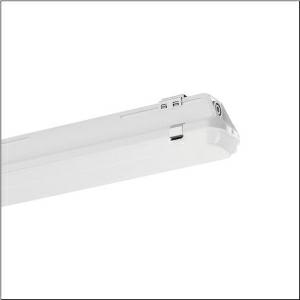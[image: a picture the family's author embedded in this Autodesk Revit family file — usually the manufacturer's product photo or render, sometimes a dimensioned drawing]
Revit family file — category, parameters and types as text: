
# Revit family: monsun_21_51fb107l440k005
name_source: partatom
category: Lighting Fixtures
units: mm (PartAtom-declared; Revit-internal decimal feet)

## family parameters
Cut with Voids When Loaded = No
Host = Face
Light Source = No
Part Type = Normal
Room Calculation Point = No
Round Connector Dimension = Use Diameter
Shared = No

## types (1)
- Monsun 21 (1 x LED, 4350 lm, 24.7 W, 4000K)
    Apparent Load = 25 VA
    CIE Flux Codes = 46 76 93 94 100
    Color Rendering = 80
    Color Temperature = 4000K
    Default Elevation = 1800 mm
    Description = Monsun 21, damp-proof luminaire, chain hanger, primary optical cover: enclosure, of PMMA, light emission: direct distribution, primary light characteristic: symmetric, installation type: vertical mounting, horizontal mounting, surface-mounted, suspended mounting, LED, rated luminous flux: 4.350lm, luminous efficacy: 176lm/W, light colour: 840, colour temperature: 4000K, control gear: ON/OFF, with terminal, 3-pole, max. 2.5mm², through-wiring: 5x 2.5mm², mains connection: 220..240V, AC, 50/60Hz, rated input power: 25W, housing, of glass-fibre reinforced plastic, uncoated, bright grey, incl. chain hanger, length: 1.299mm, width: 90mm, height: 88mm, clip for enclosure, of stainless steel (V2A), ceiling mounting element, of stainless steel (V2A), chain hanger, of stainless steel (V2A), protection rating (complete): IP66, insulation class (complete): insulation class I (protective earthing), certification: CE, ENEC, VDE, UKCA, protection symbol: D, impact resistance: IK04, permissible operating ambient temperature: -25..+35°C, standard: EN 50419, EN 60598-2-1, corresponds to IFS (International Featured Standards) requirements for safety and quality in the food industry, for indoor or canopied outdoor use, no direct snow, no direct sun, no direct rain, LABS conformity tested according to VDMA 24364:2018-05, contact your sales advisor before using the luminaires in applications with unclear chemical exposure, large temperature fluctuations or condensation-forming humidity, packaging unit: 1 piece
    Height = 88 mm
    Lamp = 1 x LED
    Lamp Light Flux = 4350 lm
    Lamp Power = 24.7 W
    Lamp count = 1
    Length = 1299 mm
    Luminous efficacy = 176 lm/W
    Manufacturer = Siteco
    ModVariant = No
    Model = 51FB107L440K005
    Mounting Place = Ceiling
    Mounting Type = Surface mounted
    Number of Poles = 1
    OnlyDefault = Yes
    Power Factor = 1
    Product Name = Monsun 21
    Product group = damp-proof luminaire
    ProductGroupID = 300
    Protection Class = Protection class I
    Protection Degree = IP 66
    RLX_Detail_Level = 1
    RLX_Emergency_Light_Flux = 0 lm
    RLX_Emergency_Type = 0
    RLX_Emergency_Type_DB = No
    RlxData = <blob elided: 89725 chars, md5=d2f577ab>
    Socket = socket
    Standby Power = 0 W
    System Light Flux = 4350 lm
    System Power = 25 W
    Type Comments = Product without accessories
    Type Image = l_1319656.jpg
    URL = http://relux.com
    VarID = ---
    Voltage = 0 V
    Weight = 0.00 kg
    Width = 90 mm

## geometry (parser evidence)
native form markers: Blend x4, Sweep x13
no freeform markers — native parametric forms only
